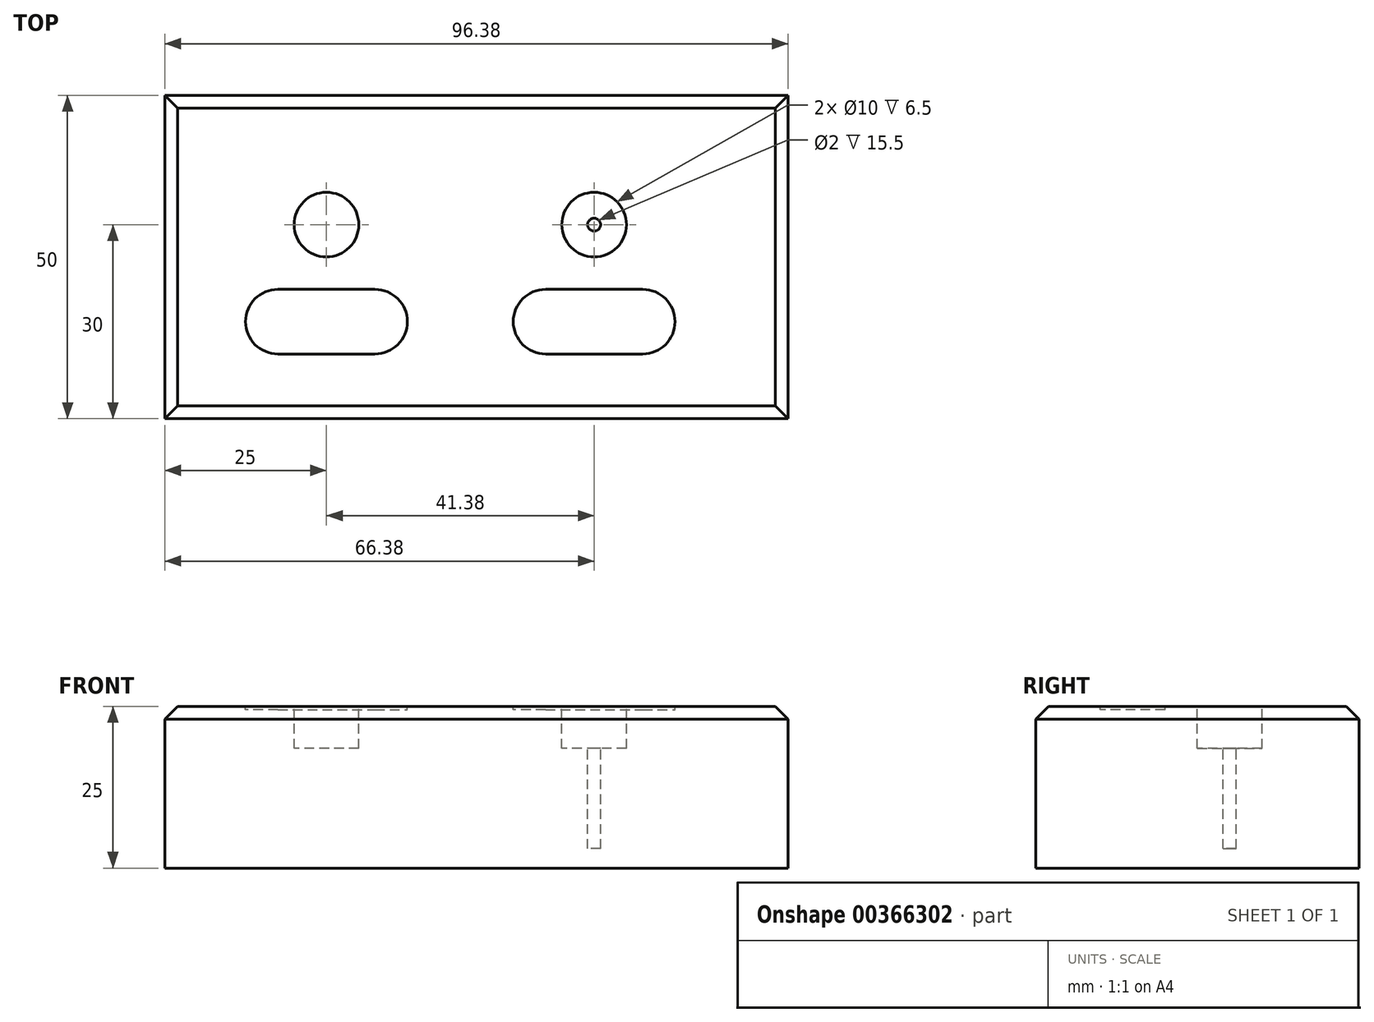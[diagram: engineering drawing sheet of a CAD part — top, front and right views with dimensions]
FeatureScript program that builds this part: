
annotation { "Feature Type Name" : "Feature", "Feature Type Description" : "" }
export const myFeature = defineFeature(function(context is Context, id is Id, definition is map)
    precondition{}
    {
        {
            var Q0;
            Q0=qCreatedBy(makeId("Top.planeOp"),FACE);
            var sketch = newSketch(context, id + "F0", { "sketchPlane" : qUnion([Q0])});
            skLineSegment(sketch, "E0.bottom", {"start": v(0, 0) * mm, "end": v(96.38, 0) * mm});
            skLineSegment(sketch, "E0.top", {"start": v(0, 50) * mm, "end": v(96.38, 50) * mm});
            skLineSegment(sketch, "E0.left", {"start": v(0, 0) * mm, "end": v(0, 50) * mm});
            skLineSegment(sketch, "E0.right", {"start": v(96.38, 0) * mm, "end": v(96.38, 50) * mm});
            skSolve(sketch);
        }
        {
            var Q0;
            Q0=makeQuery(id+"F0.imprint","IMPRINT",FACE,{"disambiguationData":[TD([[makeQuery(id+"F0.imprint","IMPRINT",EDGE,{"derivedFrom":sQuery(id+"F0.wireOp",EDGE,"E0.bottom")}),1.0]])]});
            extrude(context, id + "F1", {"entities" : qUnion([Q0]), "depth" : 25 * mm});
        }
        {
            var Q0;
            Q0=makeQuery(id+"F1.opExtrude","CAP_FACE",FACE,{"disambiguationData":[OSD([sQuery(id+"F0.wireOp",EDGE,"E0.bottom"),sQuery(id+"F0.wireOp",EDGE,"E0.top"),sQuery(id+"F0.wireOp",EDGE,"E0.left"),sQuery(id+"F0.wireOp",EDGE,"E0.right")])],"isStart":false});
            var sketch = newSketch(context, id + "F2", { "sketchPlane" : qUnion([Q0])});
            skCircle(sketch, "E1", {"center": v(25, 30) * mm, "radius": 5 * mm});
            skCircle(sketch, "E2", {"center": v(66.38, 30) * mm, "radius": 5 * mm});
            skSolve(sketch);
        }
        {
            var Q0;
            Q0=makeQuery(id+"F2.imprint","IMPRINT",FACE,{"disambiguationData":[TD([[makeQuery(id+"F2.imprint","IMPRINT",EDGE,{"derivedFrom":sQuery(id+"F2.wireOp",EDGE,"E1")}),1.0]])]});
            var Q1;
            Q1=makeQuery(id+"F2.imprint","IMPRINT",FACE,{"disambiguationData":[TD([[makeQuery(id+"F2.imprint","IMPRINT",EDGE,{"derivedFrom":sQuery(id+"F2.wireOp",EDGE,"E2")}),1.0]])]});
            extrude(context, id + "F3", {"entities" : qUnion([Q0, Q1]), "operationType" : NewBodyOperationType.REMOVE, "oppositeDirection" : true, "depth" : 6.5 * mm});
        }
        {
            var Q0;
            Q0=makeQuery(id+"F1.opExtrude","CAP_FACE",FACE,{"disambiguationData":[OSD([sQuery(id+"F0.wireOp",EDGE,"E0.bottom"),sQuery(id+"F0.wireOp",EDGE,"E0.top"),sQuery(id+"F0.wireOp",EDGE,"E0.left"),sQuery(id+"F0.wireOp",EDGE,"E0.right")])],"isStart":false});
            var sketch = newSketch(context, id + "F4", { "sketchPlane" : qUnion([Q0])});
            skCircle(sketch, "E3", {"center": v(66.38, 30) * mm, "radius": 1 * mm});
            skSolve(sketch);
        }
        {
            var Q0;
            Q0 = qSketchRegion(id + "F4", true);
            extrude(context, id + "F5", {"entities" : qUnion([Q0]), "operationType" : NewBodyOperationType.REMOVE, "oppositeDirection" : true, "depth" : 22 * mm});
        }
        {
            var Q0;
            Q0=makeQuery(id+"F1.opExtrude","CAP_EDGE",EDGE,{"disambiguationData":[OSD([sQuery(id+"F0.wireOp",EDGE,"E0.bottom")])],"isStart":false});
            var Q1;
            Q1=makeQuery(id+"F1.opExtrude","CAP_EDGE",EDGE,{"disambiguationData":[OSD([sQuery(id+"F0.wireOp",EDGE,"E0.right")])],"isStart":false});
            var Q2;
            Q2=makeQuery(id+"F1.opExtrude","CAP_EDGE",EDGE,{"disambiguationData":[OSD([sQuery(id+"F0.wireOp",EDGE,"E0.left")])],"isStart":false});
            var Q3;
            Q3=makeQuery(id+"F1.opExtrude","CAP_EDGE",EDGE,{"disambiguationData":[OSD([sQuery(id+"F0.wireOp",EDGE,"E0.top")])],"isStart":false});
            chamfer(context, id + "F6", {"entities" : qUnion([Q0, Q1, Q2, Q3]), "width" : 2 * mm, "tangentPropagation" : true});
        }
        {
            var Q0;
            Q0=makeQuery(id+"F1.opExtrude","CAP_FACE",FACE,{"disambiguationData":[OSD([sQuery(id+"F0.wireOp",EDGE,"E0.bottom"),sQuery(id+"F0.wireOp",EDGE,"E0.top"),sQuery(id+"F0.wireOp",EDGE,"E0.left"),sQuery(id+"F0.wireOp",EDGE,"E0.right")])],"isStart":false});
            var sketch = newSketch(context, id + "F7", { "sketchPlane" : qUnion([Q0])});
            skLineSegment(sketch, "E4.bottom", {"start": v(17.5, 20) * mm, "end": v(32.5, 20) * mm});
            skLineSegment(sketch, "E4.top", {"start": v(17.5, 10) * mm, "end": v(32.5, 10) * mm});
            skLineSegment(sketch, "E4.left", {"start": v(12.5, 15) * mm, "end": v(12.5, 15) * mm});
            skLineSegment(sketch, "E4.right", {"start": v(37.5, 15) * mm, "end": v(37.5, 15) * mm});
            skPoint(sketch, "E5.visualSharp", {"position": v(12.5, 20) * mm});
            skArc(sketch, "E5.filletArc", {"start": v(17.5, 20) * mm, "mid": v(13.96, 18.54) * mm, "end": v(12.5, 15) * mm});
            skPoint(sketch, "E6.visualSharp", {"position": v(37.5, 20) * mm});
            skArc(sketch, "E6.filletArc", {"start": v(37.5, 15) * mm, "mid": v(36.04, 18.54) * mm, "end": v(32.5, 20) * mm});
            skPoint(sketch, "E7.visualSharp", {"position": v(37.5, 10) * mm});
            skArc(sketch, "E7.filletArc", {"start": v(32.5, 10) * mm, "mid": v(36.04, 11.46) * mm, "end": v(37.5, 15) * mm});
            skPoint(sketch, "E8.visualSharp", {"position": v(12.5, 10) * mm});
            skArc(sketch, "E8.filletArc", {"start": v(12.5, 15) * mm, "mid": v(13.96, 11.46) * mm, "end": v(17.5, 10) * mm});
            skLineSegment(sketch, "E9.bottom", {"start": v(58.88, 20) * mm, "end": v(73.88, 20) * mm});
            skLineSegment(sketch, "E9.top", {"start": v(58.88, 10) * mm, "end": v(73.88, 10) * mm});
            skLineSegment(sketch, "E9.left", {"start": v(53.88, 15) * mm, "end": v(53.88, 15) * mm});
            skLineSegment(sketch, "E9.right", {"start": v(78.88, 15) * mm, "end": v(78.88, 15) * mm});
            skPoint(sketch, "E10.visualSharp", {"position": v(53.88, 20) * mm});
            skArc(sketch, "E10.filletArc", {"start": v(58.88, 20) * mm, "mid": v(55.34, 18.54) * mm, "end": v(53.88, 15) * mm});
            skPoint(sketch, "E11.visualSharp", {"position": v(53.88, 10) * mm});
            skArc(sketch, "E11.filletArc", {"start": v(53.88, 15) * mm, "mid": v(55.34, 11.46) * mm, "end": v(58.88, 10) * mm});
            skPoint(sketch, "E12.visualSharp", {"position": v(78.88, 10) * mm});
            skArc(sketch, "E12.filletArc", {"start": v(73.88, 10) * mm, "mid": v(77.42, 11.46) * mm, "end": v(78.88, 15) * mm});
            skPoint(sketch, "E13.visualSharp", {"position": v(78.88, 20) * mm});
            skArc(sketch, "E13.filletArc", {"start": v(78.88, 15) * mm, "mid": v(77.42, 18.54) * mm, "end": v(73.88, 20) * mm});
            skSolve(sketch);
        }
        {
            var Q0;
            Q0=makeQuery(id+"F7.imprint","IMPRINT",FACE,{"disambiguationData":[TD([[makeQuery(id+"F7.imprint","IMPRINT",EDGE,{"derivedFrom":sQuery(id+"F7.wireOp",EDGE,"E4.bottom")}),-1.0]])]});
            var Q1;
            Q1=makeQuery(id+"F7.imprint","IMPRINT",FACE,{"disambiguationData":[TD([[makeQuery(id+"F7.imprint","IMPRINT",EDGE,{"derivedFrom":sQuery(id+"F7.wireOp",EDGE,"E9.bottom")}),-1.0]])]});
            extrude(context, id + "F8", {"entities" : qUnion([Q0, Q1]), "operationType" : NewBodyOperationType.REMOVE, "oppositeDirection" : true, "depth" : 0.5 * mm});
        }
    });
